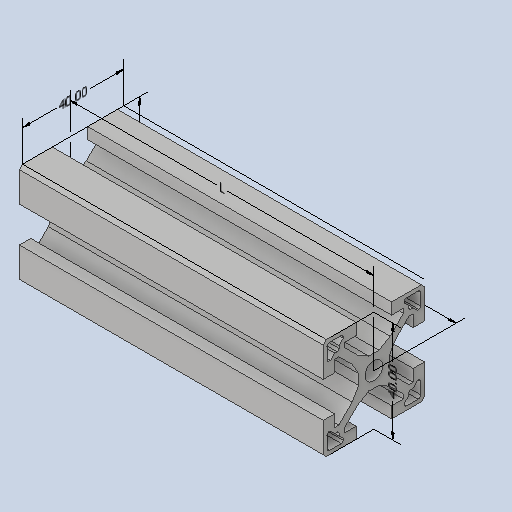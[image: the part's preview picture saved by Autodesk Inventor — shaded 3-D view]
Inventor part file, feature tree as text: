
AUTODESK INVENTOR PART (.ipt)
format: ipt  version: 2023 (Build 270158000, 158)  size: 288,768 bytes
history: native  units: mm
features: other x125, extrude x1, sketch x1
ambient origin geometry x8: Origin, YZ Plane, XZ Plane, XY Plane, X Axis, Y Axis, Z Axis, Center Point
bodies: Solid1 (feature_tree)
feature tree (127):
  other  "Annotations"
  extrude  "Extrusion1"  [1 undecoded]
  other  "CS_ANBAU_HINTEN_LINKS_XY"
  other  "CS_ANBAU_HINTEN_LINKS_YZ"
  other  "CS_ANBAU_HINTEN_LINKS_ZX"
  other  "CS_ANBAU_HINTEN_LINKS_X"
  other  "CS_ANBAU_HINTEN_LINKS_Y"
  other  "CS_ANBAU_HINTEN_LINKS_Z"
  other  "CS_ANBAU_HINTEN_LINKS_Center"
  other  "CS_ANBAU_HINTEN_OBEN_XY"
  other  "CS_ANBAU_HINTEN_OBEN_YZ"
  other  "CS_ANBAU_HINTEN_OBEN_ZX"
  other  "CS_ANBAU_HINTEN_OBEN_X"
  other  "CS_ANBAU_HINTEN_OBEN_Y"
  other  "CS_ANBAU_HINTEN_OBEN_Z"
  other  "CS_ANBAU_HINTEN_OBEN_Center"
  other  "CS_ANBAU_HINTEN_RECHTS_XY"
  other  "CS_ANBAU_HINTEN_RECHTS_YZ"
  other  "CS_ANBAU_HINTEN_RECHTS_ZX"
  other  "CS_ANBAU_HINTEN_RECHTS_X"
  other  "CS_ANBAU_HINTEN_RECHTS_Y"
  other  "CS_ANBAU_HINTEN_RECHTS_Z"
  other  "CS_ANBAU_HINTEN_RECHTS_Center"
  other  "CS_ANBAU_HINTEN_UNTEN_XY"
  other  "CS_ANBAU_HINTEN_UNTEN_YZ"
  other  "CS_ANBAU_HINTEN_UNTEN_ZX"
  other  "CS_ANBAU_HINTEN_UNTEN_X"
  other  "CS_ANBAU_HINTEN_UNTEN_Y"
  other  "CS_ANBAU_HINTEN_UNTEN_Z"
  other  "CS_ANBAU_HINTEN_UNTEN_Center"
  other  "CS_ANBAU_QUER_XY"
  other  "CS_ANBAU_QUER_YZ"
  other  "CS_ANBAU_QUER_ZX"
  other  "CS_ANBAU_QUER_X"
  other  "CS_ANBAU_QUER_Y"
  other  "CS_ANBAU_QUER_Z"
  other  "CS_ANBAU_QUER_Center"
  other  "CS_ANBAU_QUER_1_XY"
  other  "CS_ANBAU_QUER_1_YZ"
  other  "CS_ANBAU_QUER_1_ZX"
  other  "CS_ANBAU_QUER_1_X"
  other  "CS_ANBAU_QUER_1_Y"
  other  "CS_ANBAU_QUER_1_Z"
  other  "CS_ANBAU_QUER_1_Center"
  other  "CS_ANBAU_VORNE_LINKS_XY"
  other  "CS_ANBAU_VORNE_LINKS_YZ"
  other  "CS_ANBAU_VORNE_LINKS_ZX"
  other  "CS_ANBAU_VORNE_LINKS_X"
  other  "CS_ANBAU_VORNE_LINKS_Y"
  other  "CS_ANBAU_VORNE_LINKS_Z"
  other  "CS_ANBAU_VORNE_LINKS_Center"
  other  "CS_ANBAU_VORNE_OBEN_XY"
  other  "CS_ANBAU_VORNE_OBEN_YZ"
  other  "CS_ANBAU_VORNE_OBEN_ZX"
  other  "CS_ANBAU_VORNE_OBEN_X"
  other  "CS_ANBAU_VORNE_OBEN_Y"
  other  "CS_ANBAU_VORNE_OBEN_Z"
  other  "CS_ANBAU_VORNE_OBEN_Center"
  other  "CS_ANBAU_VORNE_RECHTS_XY"
  other  "CS_ANBAU_VORNE_RECHTS_YZ"
  other  "CS_ANBAU_VORNE_RECHTS_ZX"
  other  "CS_ANBAU_VORNE_RECHTS_X"
  other  "CS_ANBAU_VORNE_RECHTS_Y"
  other  "CS_ANBAU_VORNE_RECHTS_Z"
  other  "CS_ANBAU_VORNE_RECHTS_Center"
  other  "CS_ANBAU_VORNE_UNTEN_XY"
  other  "CS_ANBAU_VORNE_UNTEN_YZ"
  other  "CS_ANBAU_VORNE_UNTEN_ZX"
  other  "CS_ANBAU_VORNE_UNTEN_X"
  other  "CS_ANBAU_VORNE_UNTEN_Y"
  other  "CS_ANBAU_VORNE_UNTEN_Z"
  other  "CS_ANBAU_VORNE_UNTEN_Center"
  other  "p1_XY"
  other  "p1_YZ"
  other  "p1_ZX"
  other  "p1_X"
  other  "p1_Y"
  other  "p1_Z"
  other  "p1_Center"
  other  "p2_XY"
  other  "p2_YZ"
  other  "p2_ZX"
  other  "p2_X"
  other  "p2_Y"
  other  "p2_Z"
  other  "p2_Center"
  other  "p3_XY"
  other  "p3_YZ"
  other  "p3_ZX"
  other  "p3_X"
  other  "p3_Y"
  other  "p3_Z"
  other  "p3_Center"
  other  "p4_XY"
  other  "p4_YZ"
  other  "p4_ZX"
  other  "p4_X"
  other  "p4_Y"
  other  "p4_Z"
  other  "p4_Center"
  other  "p5_XY"
  other  "p5_YZ"
  other  "p5_ZX"
  other  "p5_X"
  other  "p5_Y"
  other  "p5_Z"
  other  "p5_Center"
  other  "pm1_XY"
  other  "pm1_YZ"
  other  "pm1_ZX"
  other  "pm1_X"
  other  "pm1_Y"
  other  "pm1_Z"
  other  "pm1_Center"
  other  "pm2_XY"
  other  "pm2_YZ"
  other  "pm2_ZX"
  other  "pm2_X"
  other  "pm2_Y"
  other  "pm2_Z"
  other  "pm2_Center"
  sketch  "Skizze_1"  dims[d0=120.0mm d1=0.0mm d2=0.0mm d3=0.0mm d4=0.0mm d5=0.0mm d6=0.0mm d10=120.0mm d11=120.0mm d7=40.0mm d8=40.0mm d9=40.0mm]
  other  "Linear Dimension 1"
  other  "Linear Dimension 2"
  other  "Linear Dimension 3"
  other  "Linear Dimension 4"
  other  "Linear Dimension 5"
note: 1 required parameter value undecoded (feature->parameter linkage not recoverable at this tier; creation-order binding heuristic only, values carry confidence <= 0.55)
